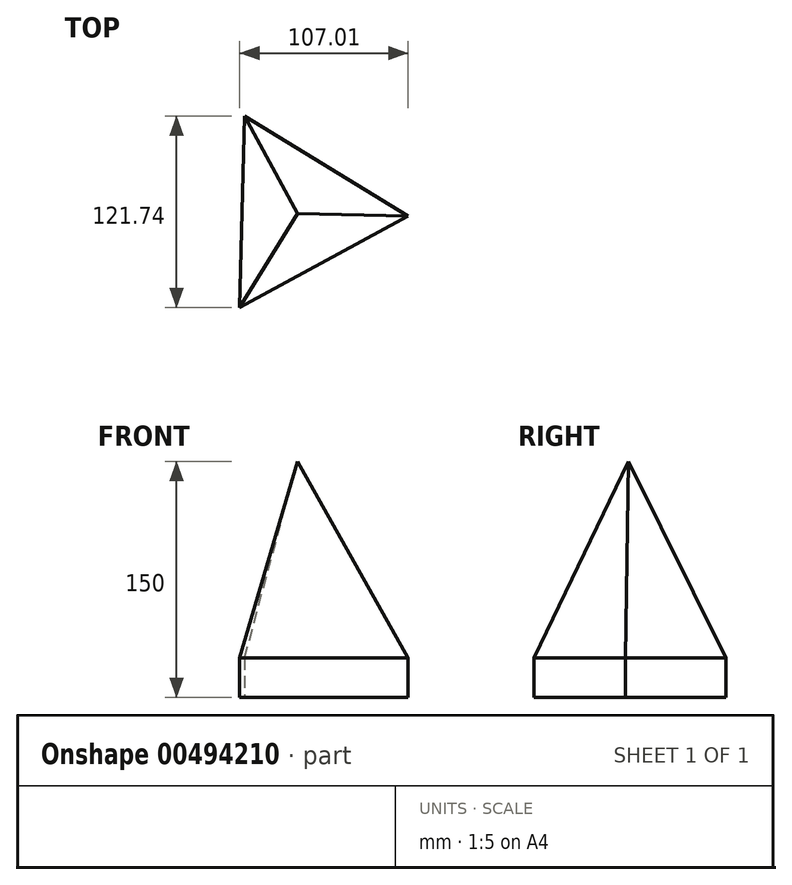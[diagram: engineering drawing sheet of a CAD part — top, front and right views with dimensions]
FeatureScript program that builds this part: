
annotation { "Feature Type Name" : "Feature", "Feature Type Description" : "" }
export const myFeature = defineFeature(function(context is Context, id is Id, definition is map)
    precondition{}
    {
        {
            var Q0;
            Q0=qCreatedBy(makeId("Top.planeOp"),FACE);
            var sketch = newSketch(context, id + "F0", { "sketchPlane" : qUnion([Q0])});
            skCircle(sketch, "E0.cCircle", {"center": v(0, 0) * mm, "radius": 35.16 * mm, "construction": true});
            skLineSegment(sketch, "E0.0", {"start": v(-33.57, 61.78) * mm, "end": v(70.29, -1.82) * mm});
            skLineSegment(sketch, "E0.1", {"start": v(70.29, -1.82) * mm, "end": v(-36.72, -59.96) * mm});
            skLineSegment(sketch, "E0.2", {"start": v(-36.72, -59.96) * mm, "end": v(-33.57, 61.78) * mm});
            skPoint(sketch, "E0.0.midPoint", {"position": v(18.36, 29.98) * mm});
            skSolve(sketch);
        }
        {
            var Q0;
            Q0=makeQuery(id+"F0.imprint","IMPRINT",FACE,{"disambiguationData":[TD([[makeQuery(id+"F0.imprint","IMPRINT",EDGE,{"derivedFrom":sQuery(id+"F0.wireOp",EDGE,"E0.0")}),-1.0]])]});
            extrude(context, id + "F1", {"entities" : qUnion([Q0]), "depth" : 25 * mm});
        }
        {
            var Q0;
            Q0=qCreatedBy(makeId("Top.planeOp"),FACE);
            cPlane(context, id + "F2", {"entities" : qUnion([Q0]), "cplaneType" : CPlaneType.OFFSET, "offset" : 150 * mm, "width" : 150 * mm, "height" : 150 * mm});
        }
        {
            var Q0;
            Q0=qCreatedBy(id+"F2.planeOp",FACE);
            var sketch = newSketch(context, id + "F3", { "sketchPlane" : qUnion([Q0])});
            skPoint(sketch, "E1", {"position": v(0, 0) * mm});
            skSolve(sketch);
        }
        {
            var Q1;
            Q1=makeQuery(id+"F1.opExtrude","CAP_FACE",FACE,{"disambiguationData":[OSD([sQuery(id+"F0.wireOp",EDGE,"E0.0"),sQuery(id+"F0.wireOp",EDGE,"E0.1"),sQuery(id+"F0.wireOp",EDGE,"E0.2")])],"isStart":false});
            var Q2;
            Q2=sQuery(id+"F3.wireOp",VERTEX,"E1");
            loft(context, id + "F4", {"operationType" : NewBodyOperationType.ADD, "sheetProfilesArray" : [{ "sheetProfileEntities" : qUnion([Q1]) }, { "sheetProfileEntities" : qUnion([Q2]) }]});
        }
    });
